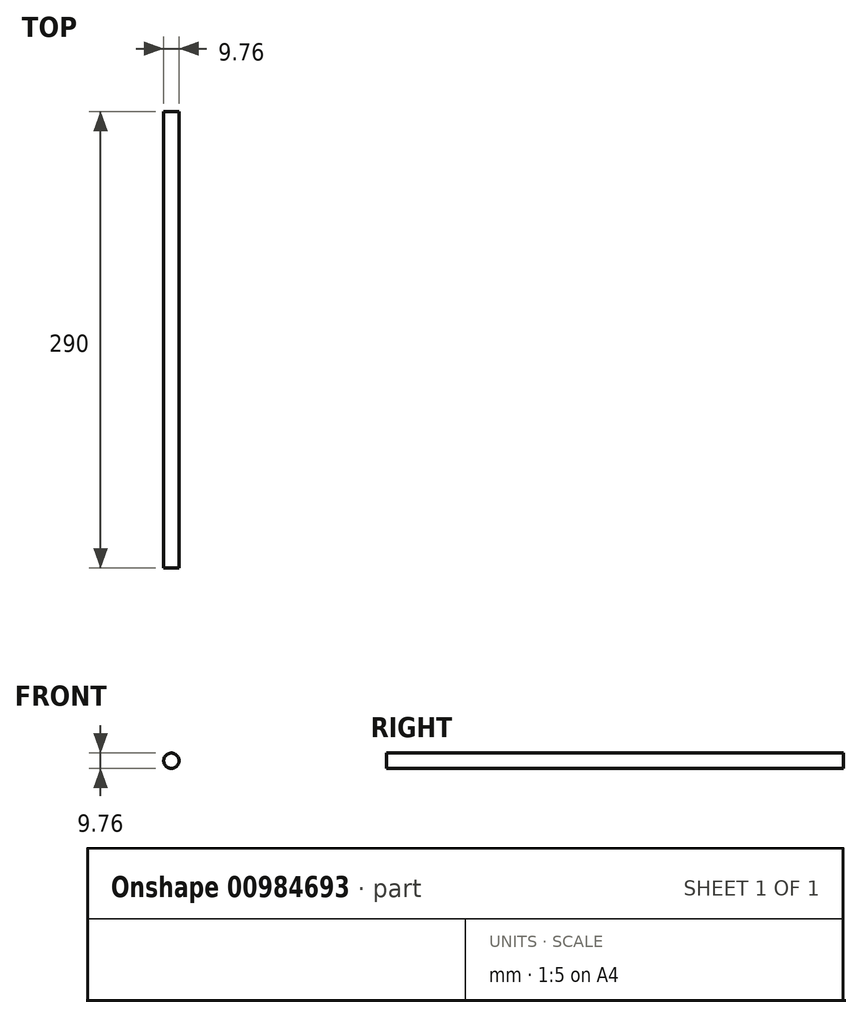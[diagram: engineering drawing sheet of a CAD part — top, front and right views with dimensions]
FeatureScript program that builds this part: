
annotation { "Feature Type Name" : "Feature", "Feature Type Description" : "" }
export const myFeature = defineFeature(function(context is Context, id is Id, definition is map)
    precondition{}
    {
        {
            var Q0;
            Q0=qCreatedBy(makeId("Front.planeOp"),FACE);
            var sketch = newSketch(context, id + "F0", { "sketchPlane" : qUnion([Q0])});
            skCircle(sketch, "E0", {"center": v(0, 0) * mm, "radius": 4.88 * mm});
            skSolve(sketch);
        }
        {
            var Q0;
            Q0=makeQuery(id+"F0.imprint","IMPRINT",FACE,{"disambiguationData":[TD([[makeQuery(id+"F0.imprint","IMPRINT",EDGE,{"derivedFrom":sQuery(id+"F0.wireOp",EDGE,"E0")}),1.0]])]});
            extrude(context, id + "F1", {"entities" : qUnion([Q0]), "depth" : 290 * mm, "offsetDistance" : 25 * mm});
        }
    });
